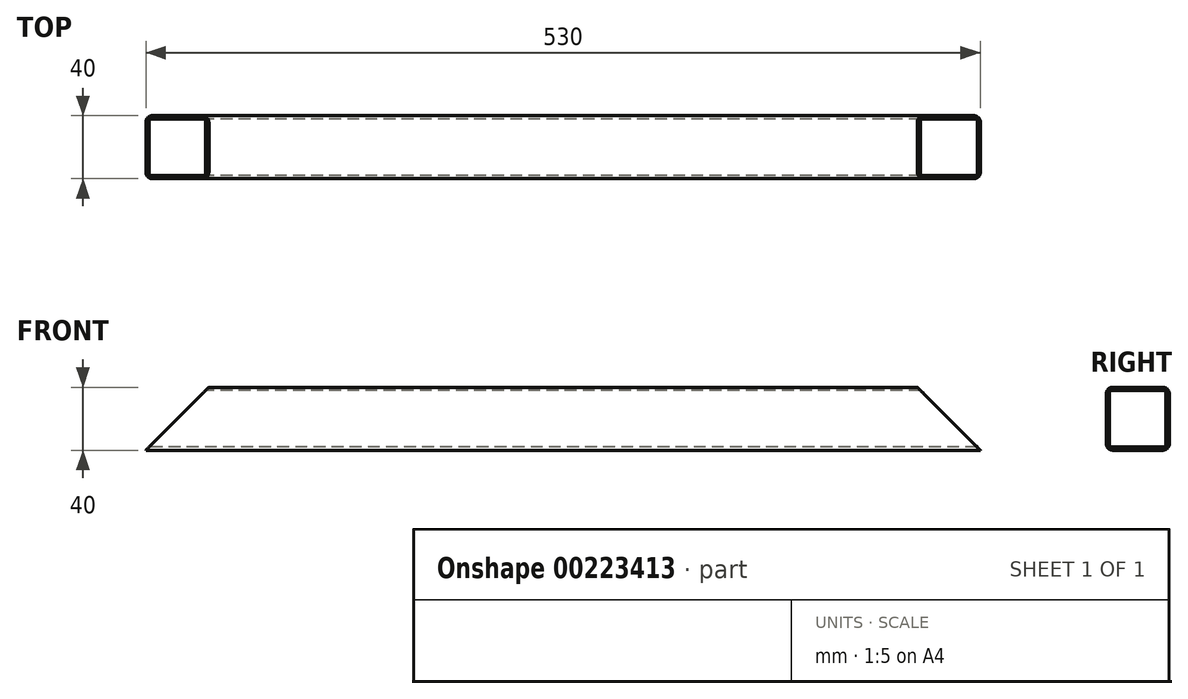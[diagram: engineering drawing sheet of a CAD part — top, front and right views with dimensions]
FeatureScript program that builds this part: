
annotation { "Feature Type Name" : "Feature", "Feature Type Description" : "" }
export const myFeature = defineFeature(function(context is Context, id is Id, definition is map)
    precondition{}
    {
        {
            var Q0;
            Q0=qCreatedBy(makeId("Right.planeOp"),FACE);
            var sketch = newSketch(context, id + "F0", { "sketchPlane" : qUnion([Q0])});
            skLineSegment(sketch, "E0.bottom", {"start": v(-4, 0) * mm, "end": v(-36, 0) * mm});
            skLineSegment(sketch, "E0.top", {"start": v(-4, 40) * mm, "end": v(-36, 40) * mm});
            skLineSegment(sketch, "E0.left", {"start": v(0, 4) * mm, "end": v(0, 36) * mm});
            skLineSegment(sketch, "E0.right", {"start": v(-40, 4) * mm, "end": v(-40, 36) * mm});
            skPoint(sketch, "E1.visualSharp", {"position": v(0, 40) * mm});
            skArc(sketch, "E1.filletArc", {"start": v(0, 36) * mm, "mid": v(-1.17, 38.83) * mm, "end": v(-4, 40) * mm});
            skPoint(sketch, "E2.visualSharp", {"position": v(-40, 40) * mm});
            skArc(sketch, "E2.filletArc", {"start": v(-36, 40) * mm, "mid": v(-38.83, 38.83) * mm, "end": v(-40, 36) * mm});
            skPoint(sketch, "E3.visualSharp", {"position": v(-40, 0) * mm});
            skArc(sketch, "E3.filletArc", {"start": v(-40, 4) * mm, "mid": v(-38.83, 1.17) * mm, "end": v(-36, 0) * mm});
            skPoint(sketch, "E4.visualSharp", {"position": v(0, 0) * mm});
            skArc(sketch, "E4.filletArc", {"start": v(-4, 0) * mm, "mid": v(-1.17, 1.17) * mm, "end": v(0, 4) * mm});
            skLineSegment(sketch, "E5.0", {"start": v(-38, 2) * mm, "end": v(-38, 38) * mm});
            skLineSegment(sketch, "E5.1", {"start": v(-2, 2) * mm, "end": v(-38, 2) * mm});
            skLineSegment(sketch, "E5.2", {"start": v(-2, 2) * mm, "end": v(-2, 38) * mm});
            skLineSegment(sketch, "E5.3", {"start": v(-2, 38) * mm, "end": v(-38, 38) * mm});
            skSolve(sketch);
        }
        {
            var Q0;
            Q0 = qSketchRegion(id + "F0", true);
            extrude(context, id + "F1", {"entities" : qUnion([Q0]), "depth" : 530 * mm});
        }
        {
            var Q0;
            Q0=makeQuery(id+"F1.opExtrude","SWEPT_FACE",FACE,{"disambiguationData":[OSD([sQuery(id+"F0.wireOp",EDGE,"E0.right")])]});
            var sketch = newSketch(context, id + "F2", { "sketchPlane" : qUnion([Q0])});
            skLineSegment(sketch, "E6", {"start": v(0, 0) * mm, "end": v(0, 45.93) * mm});
            skLineSegment(sketch, "E7", {"start": v(0, 45.93) * mm, "end": v(45.93, 45.93) * mm});
            skLineSegment(sketch, "E8", {"start": v(45.93, 45.93) * mm, "end": v(0, 0) * mm});
            skLineSegment(sketch, "E9", {"start": v(530, 0) * mm, "end": v(530, 54.87) * mm});
            skLineSegment(sketch, "E10", {"start": v(530, 54.87) * mm, "end": v(475.13, 54.87) * mm});
            skLineSegment(sketch, "E11", {"start": v(475.13, 54.87) * mm, "end": v(530, 0) * mm});
            skSolve(sketch);
        }
        {
            var Q0;
            Q0 = qSketchRegion(id + "F2", true);
            extrude(context, id + "F3", {"entities" : qUnion([Q0]), "operationType" : NewBodyOperationType.REMOVE, "endBound" : BoundingType.THROUGH_ALL, "oppositeDirection" : true, "depth" : 100 * mm});
        }
    });
